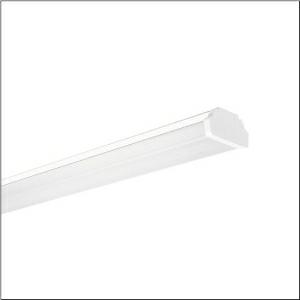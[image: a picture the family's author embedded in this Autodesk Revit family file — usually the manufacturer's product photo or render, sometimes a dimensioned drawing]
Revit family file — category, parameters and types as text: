
# Revit family: dus_31_gen_2_53bd811dv4d5d2_75d9
name_source: partatom
category: Lighting Fixtures
units: mm (PartAtom-declared; Revit-internal decimal feet)

## family parameters
Cut with Voids When Loaded = No
Host = Face
Light Source = No
Part Type = Normal
Room Calculation Point = No
Round Connector Dimension = Use Diameter
Shared = No

## types (1)
- --- (1 x LED, 13680 lm, 74.9 W, 4000K)
    Apparent Load = 75 VA
    CIE Flux Codes = 50 78 94 90 100
    Color Rendering = 80
    Color Temperature = 4000K
    Default Elevation = 1800 mm
    Description = DUS 31 Gen.2, luminaire insert, of sheet steel, coil coated, white, length: 1.535mm, width: 81mm, height: 90mm, 5x system unit, system units: 307mm, LED rated luminous flux: 13.680lm, light colour: 840, SDCM (Standard Deviation of Colour Matching)MacAdam ≤ 3 SDCM (initial), control gear: DALI 2, control gear: ECG DALI, with plug, 5-pole, with phase selection, mains connection: 220..240V, AC, 50/60Hz, rated input power: 75W, through-wiring accessed according to module size, primary optical cover: cover, of PMMA, light emission: direct distribution, primary light characteristic: symmetric, protection rating (complete): IP20, protection rating (LED compartment): IP50, insulation class (complete): insulation class I (protective earthing), certification: CE, ENEC, VDE, UKCA, impact resistance: IK03, permissible ambient temperature for indoor applications: -25..+35°C, corresponds to IFS (International Featured Standards) requirements for safety and quality in the food industry, reducing of maximum allowable ambient temperature of 5°C with ceiling mounting, packaging unit: 1 piece
    Height = 95 mm
    Lamp = 1 x LED
    Lamp Light Flux = 13680 lm
    Lamp Power = 74.9 W
    Lamp count = 1
    Length = 1535 mm
    Luminous efficacy = 183 lm/W
    Manufacturer = Siteco
    ModVariant = No
    Model = 53BD811DV4D5D2
    Mounting Place = Ceiling
    Mounting Type = Pendant
    Number of Poles = 1
    OnlyDefault = Yes
    Power Factor = 1
    Product Name = DUS 31 Gen.2
    Product group = luminaire insert | ceiling pendant
    ProductGroupID = 901
    Protection Class = Protection class I
    Protection Degree = IP 20
    RLX_Detail_Level = 1
    RLX_Emergency_Light_Flux = 0 lm
    RLX_Emergency_Type = 0
    RLX_Emergency_Type_DB = No
    RlxData = <blob elided: 32337 chars, md5=bdd39090>
    Socket = socket
    Standby Power = 0 W
    System Light Flux = 13680 lm
    System Power = 75 W
    Type Comments = factory setting: luminous flux: 100 % | dim-lin: 254 | 511 mA
    Type Image = l_1319596.jpg
    URL = http://relux.com
    VarID = @adj_050179
    Voltage = 0 V
    Weight = 0.00 kg
    Width = 81 mm

## geometry (parser evidence)
native form markers: Blend x4, Sweep x14
no freeform markers — native parametric forms only
